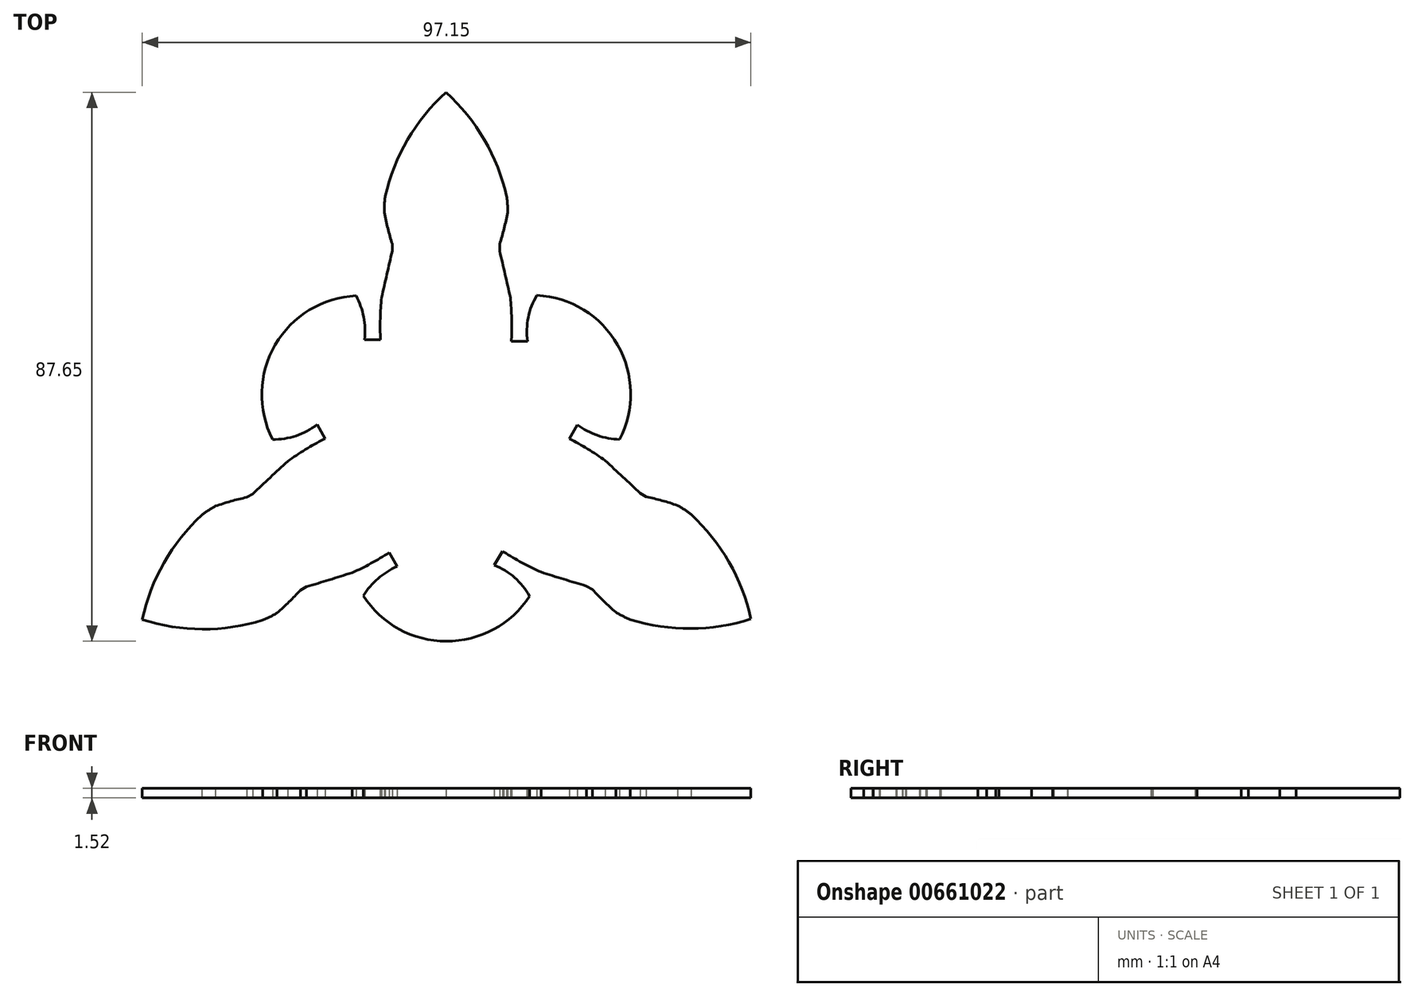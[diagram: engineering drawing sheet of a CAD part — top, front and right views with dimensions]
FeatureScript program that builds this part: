
annotation { "Feature Type Name" : "Feature", "Feature Type Description" : "" }
export const myFeature = defineFeature(function(context is Context, id is Id, definition is map)
    precondition{}
    {
        {
            var Q0;
            Q0=qCreatedBy(makeId("Top.planeOp"),FACE);
            var sketch = newSketch(context, id + "F0", { "sketchPlane" : qUnion([Q0])});
            skLineSegment(sketch, "E0", {"start": v(0, 0) * mm, "end": v(0, 11.93) * mm});
            skPoint(sketch, "E1.center", {"position": v(0, 0) * mm});
            skArc(sketch, "E2", {"start": v(-27.74, 0.68) * mm, "mid": v(-23.98, 1.25) * mm, "end": v(-20.64, 3.07) * mm});
            skArc(sketch, "E3", {"start": v(-13.05, 16.62) * mm, "mid": v(-13.2, 20.22) * mm, "end": v(-14.4, 23.61) * mm});
            skArc(sketch, "E4", {"start": v(-14.4, 23.61) * mm, "mid": v(-27.32, 15.79) * mm, "end": v(-27.74, 0.68) * mm});
            skArc(sketch, "E5.1.1", {"start": v(-7.87, -19.6) * mm, "mid": v(-10.9, -21.55) * mm, "end": v(-13.25, -24.27) * mm});
            skArc(sketch, "E5.1.2", {"start": v(-13.25, -24.27) * mm, "mid": v(-0.01, -31.56) * mm, "end": v(13.28, -24.37) * mm});
            skArc(sketch, "E5.1.3", {"start": v(13.28, -24.37) * mm, "mid": v(10.9, -21.4) * mm, "end": v(7.66, -19.4) * mm});
            skArc(sketch, "E5.2.1", {"start": v(20.92, 2.99) * mm, "mid": v(24.11, 1.33) * mm, "end": v(27.65, 0.66) * mm});
            skArc(sketch, "E5.2.2", {"start": v(27.65, 0.66) * mm, "mid": v(27.33, 15.77) * mm, "end": v(14.46, 23.68) * mm});
            skArc(sketch, "E5.2.3", {"start": v(14.46, 23.68) * mm, "mid": v(13.08, 20.14) * mm, "end": v(12.98, 16.34) * mm});
            skLineSegment(sketch, "E6", {"start": v(-13.05, 16.62) * mm, "end": v(12.98, 16.34) * mm});
            skPoint(sketch, "E7", {"position": v(-10.51, 16.6) * mm});
            skPoint(sketch, "E8", {"position": v(10.34, 16.37) * mm});
            skPoint(sketch, "E9", {"position": v(-0.06, 56.09) * mm});
            skArc(sketch, "E10", {"start": v(-0.06, 56.09) * mm, "mid": v(-6.18, 48.54) * mm, "end": v(-9.75, 39.5) * mm});
            skArc(sketch, "E11", {"start": v(-9.75, 39.5) * mm, "mid": v(-9.88, 38.2) * mm, "end": v(-9.9, 36.91) * mm});
            skArc(sketch, "E12", {"start": v(-9.9, 36.91) * mm, "mid": v(-9.34, 34.37) * mm, "end": v(-8.62, 31.87) * mm});
            skArc(sketch, "E13", {"start": v(-10.33, 23.35) * mm, "mid": v(-10.55, 19.97) * mm, "end": v(-10.51, 16.6) * mm});
            skArc(sketch, "E14", {"start": v(-8.62, 30.76) * mm, "mid": v(-9.49, 27.05) * mm, "end": v(-10.33, 23.35) * mm});
            skLineSegment(sketch, "E15", {"start": v(-0.06, 56.09) * mm, "end": v(-0.06, 55) * mm});
            skArc(sketch, "E16.MirrorCS", {"start": v(-0.06, 56.09) * mm, "mid": v(6.07, 48.54) * mm, "end": v(9.64, 39.5) * mm});
            skArc(sketch, "E17.MirrorCS", {"start": v(9.64, 39.5) * mm, "mid": v(9.77, 38.2) * mm, "end": v(9.79, 36.91) * mm});
            skArc(sketch, "E18.MirrorCS", {"start": v(9.79, 36.91) * mm, "mid": v(9.23, 34.37) * mm, "end": v(8.5, 31.87) * mm});
            skArc(sketch, "E19.MirrorCS", {"start": v(8.5, 30.76) * mm, "mid": v(9.37, 27.05) * mm, "end": v(10.21, 23.35) * mm});
            skArc(sketch, "E20.MirrorCS", {"start": v(10.21, 23.35) * mm, "mid": v(10.43, 19.97) * mm, "end": v(10.4, 16.6) * mm});
            skLineSegment(sketch, "E21", {"start": v(7.66, -19.4) * mm, "end": v(20.92, 2.99) * mm});
            skLineSegment(sketch, "E22", {"start": v(-7.87, -19.6) * mm, "end": v(-20.64, 3.07) * mm});
            skArc(sketch, "E23.1.0", {"start": v(-48.55, -28.1) * mm, "mid": v(-38.94, -29.63) * mm, "end": v(-29.33, -28.2) * mm});
            skArc(sketch, "E23.1.1", {"start": v(-48.55, -28.1) * mm, "mid": v(-45.07, -19.02) * mm, "end": v(-39.02, -11.4) * mm});
            skArc(sketch, "E23.1.2", {"start": v(-30.89, -8.01) * mm, "mid": v(-28.12, -5.4) * mm, "end": v(-25.32, -2.83) * mm});
            skArc(sketch, "E23.1.3", {"start": v(-25.32, -2.83) * mm, "mid": v(-22.51, -0.95) * mm, "end": v(-19.57, 0.7) * mm});
            skArc(sketch, "E23.1.4", {"start": v(-36.86, -9.98) * mm, "mid": v(-34.38, -9.2) * mm, "end": v(-31.85, -8.57) * mm});
            skArc(sketch, "E23.1.5", {"start": v(-39.02, -11.4) * mm, "mid": v(-37.97, -10.65) * mm, "end": v(-36.86, -9.98) * mm});
            skArc(sketch, "E23.1.6", {"start": v(-27.01, -27.03) * mm, "mid": v(-25.1, -25.28) * mm, "end": v(-23.3, -23.4) * mm});
            skArc(sketch, "E23.1.7", {"start": v(-29.33, -28.2) * mm, "mid": v(-28.15, -27.66) * mm, "end": v(-27.01, -27.03) * mm});
            skArc(sketch, "E23.1.8", {"start": v(-22.33, -22.84) * mm, "mid": v(-18.69, -21.75) * mm, "end": v(-15.05, -20.62) * mm});
            skArc(sketch, "E23.1.9", {"start": v(-15.05, -20.62) * mm, "mid": v(-12.02, -19.12) * mm, "end": v(-9.11, -17.4) * mm});
            skLineSegment(sketch, "E23.1.10", {"start": v(-23.3, -23.4) * mm, "end": v(-22.33, -22.84) * mm});
            skArc(sketch, "E23.2.0", {"start": v(48.6, -28) * mm, "mid": v(45.13, -18.91) * mm, "end": v(39.08, -11.3) * mm});
            skArc(sketch, "E23.2.1", {"start": v(48.6, -28) * mm, "mid": v(39, -29.52) * mm, "end": v(29.39, -28.1) * mm});
            skArc(sketch, "E23.2.2", {"start": v(22.38, -22.74) * mm, "mid": v(18.74, -21.65) * mm, "end": v(15.11, -20.52) * mm});
            skArc(sketch, "E23.2.3", {"start": v(15.11, -20.52) * mm, "mid": v(12.08, -19.02) * mm, "end": v(9.17, -17.3) * mm});
            skArc(sketch, "E23.2.4", {"start": v(27.07, -26.93) * mm, "mid": v(25.15, -25.18) * mm, "end": v(23.35, -23.3) * mm});
            skArc(sketch, "E23.2.5", {"start": v(29.39, -28.1) * mm, "mid": v(28.2, -27.56) * mm, "end": v(27.07, -26.93) * mm});
            skArc(sketch, "E23.2.6", {"start": v(36.92, -9.88) * mm, "mid": v(34.44, -9.1) * mm, "end": v(31.91, -8.47) * mm});
            skArc(sketch, "E23.2.7", {"start": v(39.08, -11.3) * mm, "mid": v(38.03, -10.54) * mm, "end": v(36.92, -9.88) * mm});
            skArc(sketch, "E23.2.8", {"start": v(30.95, -7.91) * mm, "mid": v(28.18, -5.3) * mm, "end": v(25.38, -2.73) * mm});
            skArc(sketch, "E23.2.9", {"start": v(25.38, -2.73) * mm, "mid": v(22.57, -0.85) * mm, "end": v(19.63, 0.8) * mm});
            skLineSegment(sketch, "E23.2.10", {"start": v(31.91, -8.47) * mm, "end": v(30.95, -7.91) * mm});
            skLineSegment(sketch, "E24", {"start": v(8.5, 31.87) * mm, "end": v(8.5, 30.76) * mm});
            skLineSegment(sketch, "E25", {"start": v(22.38, -22.74) * mm, "end": v(23.35, -23.3) * mm});
            skLineSegment(sketch, "E26", {"start": v(-30.89, -8.01) * mm, "end": v(-31.85, -8.57) * mm});
            skLineSegment(sketch, "E27", {"start": v(-8.62, 31.87) * mm, "end": v(-8.62, 30.76) * mm});
            skLineSegment(sketch, "E28", {"start": v(10.4, 16.6) * mm, "end": v(10.4, 16.37) * mm});
            skLineSegment(sketch, "E29", {"start": v(9.17, -17.3) * mm, "end": v(8.98, -17.19) * mm});
            skLineSegment(sketch, "E30", {"start": v(-19.57, 0.7) * mm, "end": v(-19.37, 0.81) * mm});
            skSolve(sketch);
        }
        {
            var Q0;
            Q0=makeQuery(id+"F0.imprint","IMPRINT",FACE,{"disambiguationData":[TD([[makeQuery(id+"F0.imprint","IMPRINT",EDGE,{"derivedFrom":sQuery(id+"F0.wireOp",EDGE,"E10")}),1.0]])]});
            var Q1;
            {var subQ6=sQuery(id+"F0.wireOp",EDGE,"E2");Q1=makeQuery(id+"F0.imprint","IMPRINT",FACE,{"disambiguationData":[TD([[makeQuery(id+"F0.imprint","IMPRINT",EDGE,{"derivedFrom":subQ6}),1.0]])]});}
            var Q2;
            Q2=makeQuery(id+"F0.imprint","IMPRINT",FACE,{"disambiguationData":[TD([[makeQuery(id+"F0.imprint","IMPRINT",EDGE,{"derivedFrom":sQuery(id+"F0.wireOp",EDGE,"E23.1.0")}),1.0]])]});
            var Q3;
            Q3=makeQuery(id+"F0.imprint","IMPRINT",FACE,{"disambiguationData":[TD([[makeQuery(id+"F0.imprint","IMPRINT",EDGE,{"derivedFrom":sQuery(id+"F0.wireOp",EDGE,"E23.2.0")}),1.0]])]});
            extrude(context, id + "F1", {"entities" : qUnion([Q0, Q1, Q2, Q3]), "depth" : 1.52 * mm, "offsetDistance" : 25.4 * mm});
        }
    });
